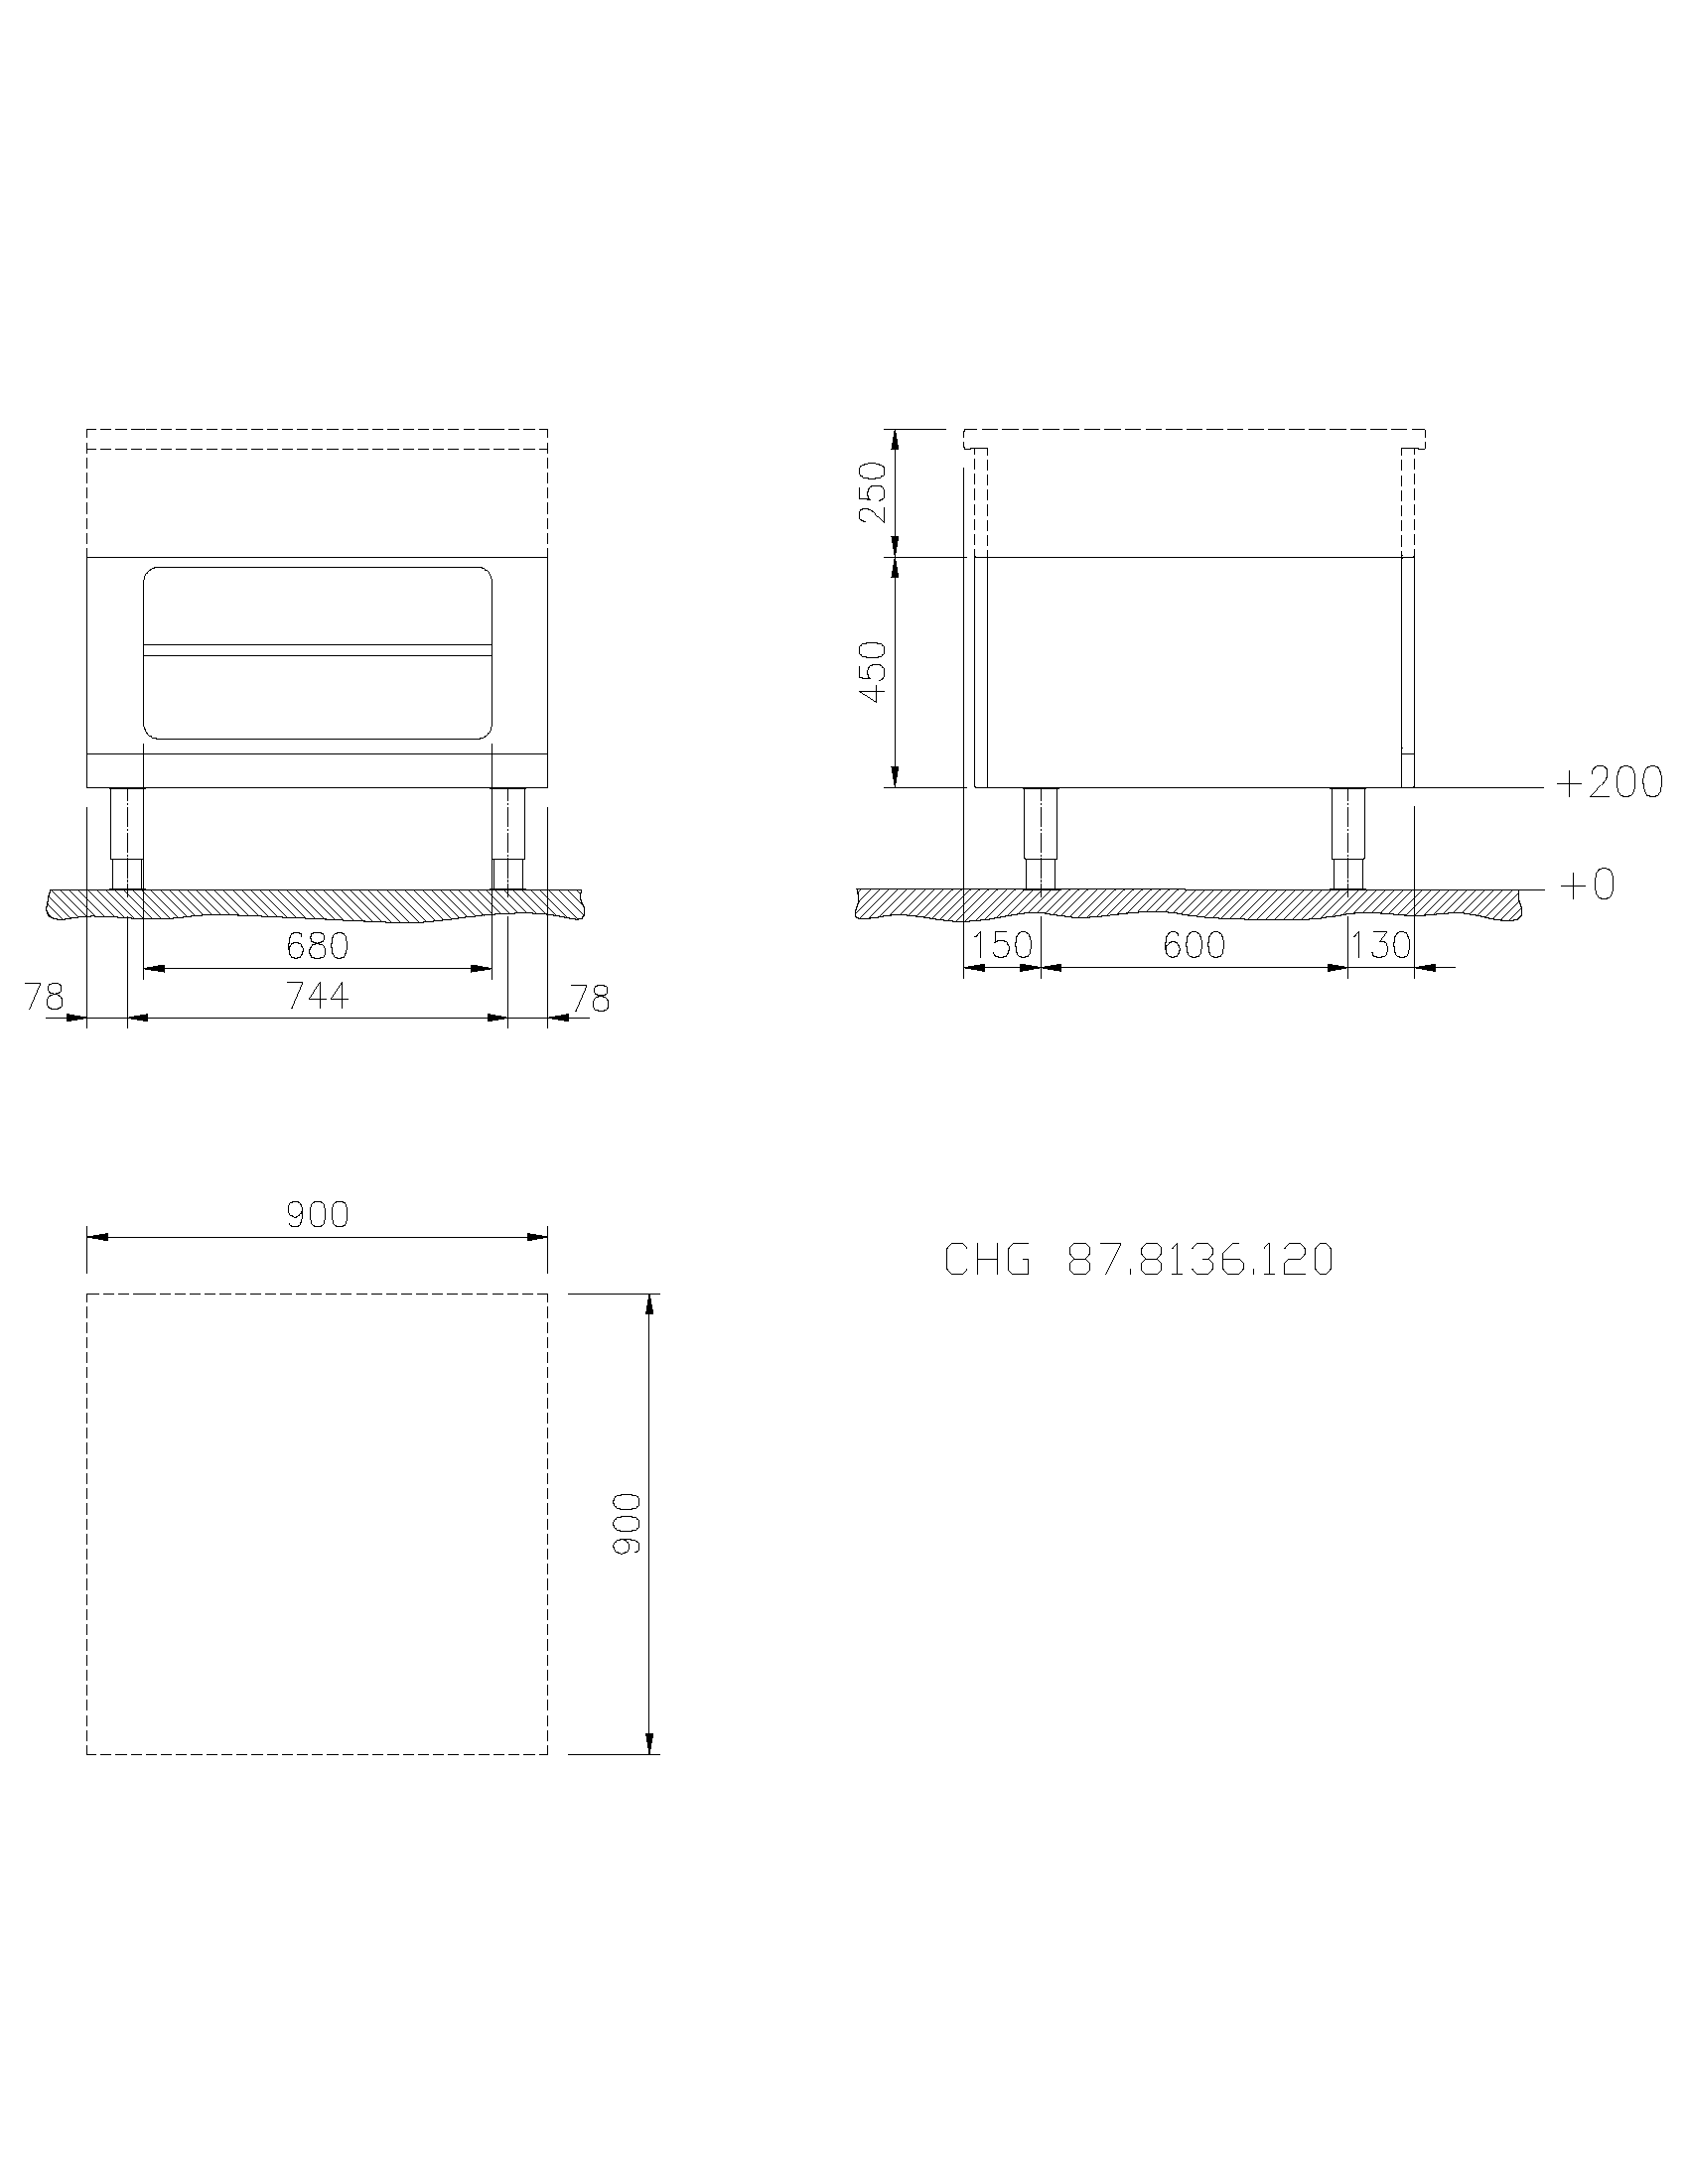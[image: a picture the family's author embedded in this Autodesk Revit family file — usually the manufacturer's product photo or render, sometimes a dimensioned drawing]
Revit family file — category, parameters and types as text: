
# Revit family: QF_ELECTROLUXPROFESSIONAL_593338_MCKDEADDVO
name_source: partatom
category: Specialty Equipment
units: mm (PartAtom-declared; Revit-internal decimal feet)

## family parameters
Always vertical = Yes
Cut with Voids When Loaded = No
Enable Cutting in Views = No
Maintain Annotation Orientation = No
Part Type = Normal
Room Calculation Point = No
Round Connector Dimension = Use Diameter
Shared = No
Work Plane-Based = No

## types (1)
- Standard
    Accessory = No
    Cold Water Size = 1"
    Compressed Air Pressure = 0.00 psi
    Compressed Air Size = 0"
    Compressed Air Volume = 0 GPM
    Condensate Return Size = 0"
    Cycle = 50 Hz
    Default Elevation = 0 mm  [stored 0 ft]
    Depth Actual = 900 mm  [stored 2.95276 ft]
    Description = GAS PASTA COOKER, TOWNGAS, 24,5L, 1-SIDE, 400X900X700H
    Direct Waste Size = 1"
    Gas Input Pressure = 2.5
    Gas KW = 9.5
    Gas Size = 1"
    HP = 0 HP
    Height Actual = 700 mm  [stored 2.29659 ft]
    Hot Water Size = 0"
    Item Number = 593338
    Length Actual = 400 mm  [stored 1.31234 ft]
    Manufacturer = Electrolux Professional
    Model = MCKDEADDVO
    Phase = 3
    Refrigerant Compressor Remote = Yes
    Refrigeration Liquid Line Size = 0 mm  [stored 0 ft]
    Refrigeration Suction Line Size = 0 mm  [stored 0 ft]
    Steam Consumption per Hour = 0
    Steam Supply Maximum Pressure = 0.00 psi
    Steam Supply Minimum Pressure = 0.00 psi
    Steam Supply Size = 0"
    URL = http://www.electroluxprofessional.com
    URL Manufacturer = http://www.electroluxprofessional.com
    Volts = 440 V
    Watts = 0 W
    Weight = 73.00 kg

note: source unit labels omitted for Gas Input Pressure — the stored unit's dimension contradicts the parameter name (converter mislabeling)

note: [stored X ft] marks values corroborated as IEEE doubles in the binary element streams (Revit-internal decimal feet)

## geometry (parser evidence)
native form markers: Blend x4, Sweep x11
no freeform markers — native parametric forms only
